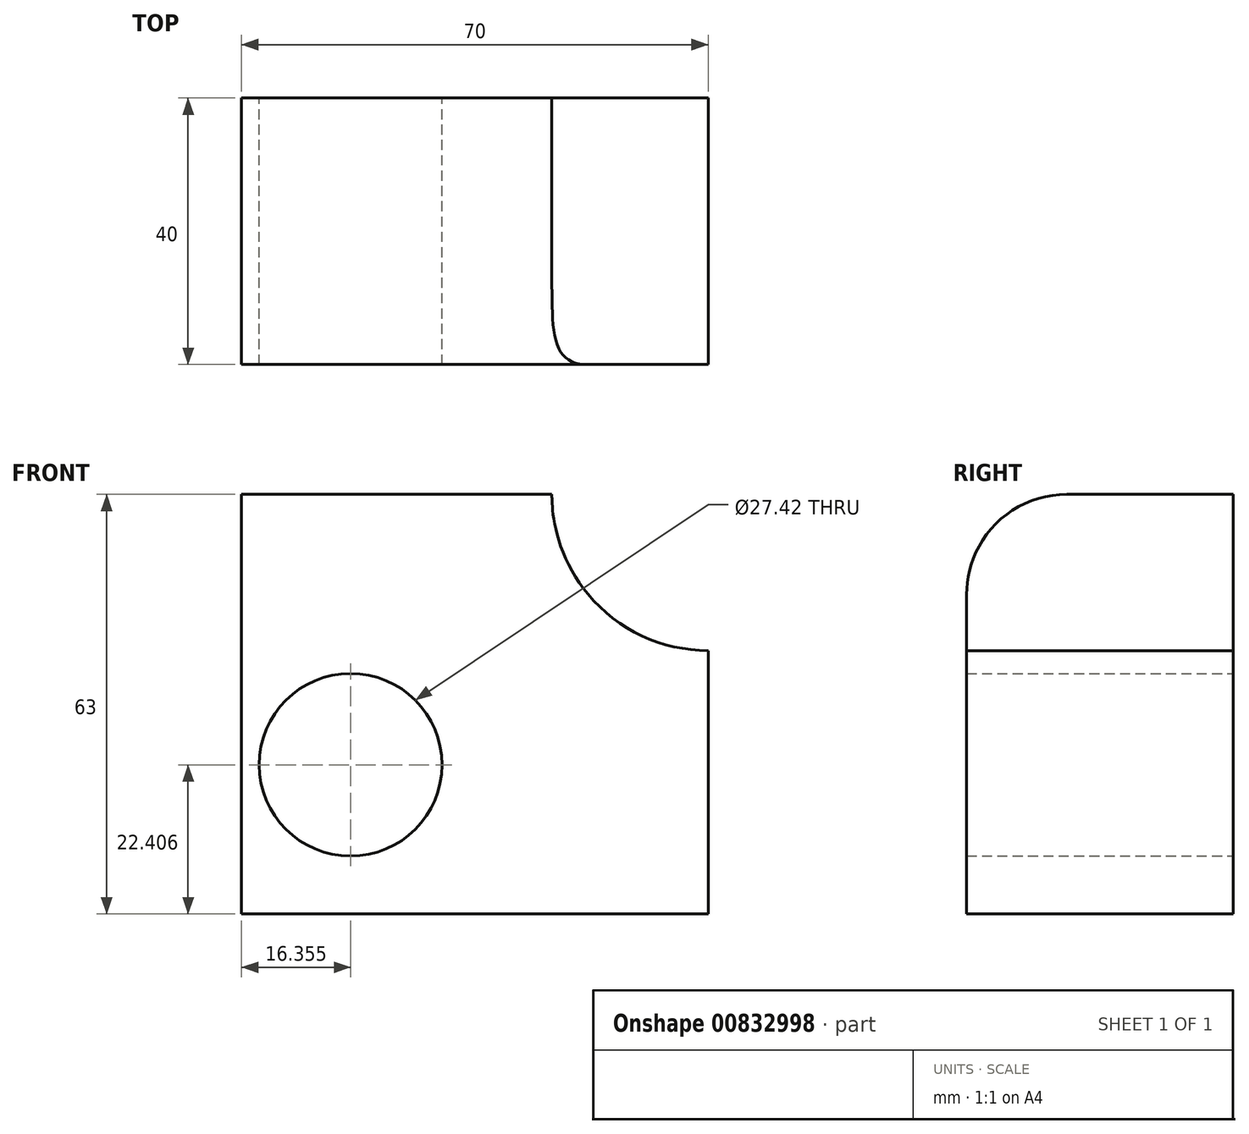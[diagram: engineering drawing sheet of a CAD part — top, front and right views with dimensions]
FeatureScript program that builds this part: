
annotation { "Feature Type Name" : "Feature", "Feature Type Description" : "" }
export const myFeature = defineFeature(function(context is Context, id is Id, definition is map)
    precondition{}
    {
        {
            var Q0;
            Q0=qCreatedBy(makeId("Top.planeOp"),FACE);
            var sketch = newSketch(context, id + "F0", { "sketchPlane" : qUnion([Q0])});
            skLineSegment(sketch, "E0.bottom", {"start": v(-35, -6) * mm, "end": v(35, -6) * mm});
            skLineSegment(sketch, "E0.top", {"start": v(-35, -46) * mm, "end": v(35, -46) * mm});
            skLineSegment(sketch, "E0.left", {"start": v(-35, -6) * mm, "end": v(-35, -46) * mm});
            skLineSegment(sketch, "E0.right", {"start": v(35, -6) * mm, "end": v(35, -46) * mm});
            skSolve(sketch);
        }
        {
            var Q0;
            Q0 = qSketchRegion(id + "F0", true);
            extrude(context, id + "F1", {"entities" : qUnion([Q0]), "depth" : 63 * mm, "offsetDistance" : 25 * mm});
        }
        {
            var Q0;
            Q0=makeQuery(id+"F1.opExtrude","SWEPT_FACE",FACE,{"disambiguationData":[OSD([sQuery(id+"F0.wireOp",EDGE,"E0.top")])]});
            var sketch = newSketch(context, id + "F2", { "sketchPlane" : qUnion([Q0])});
            skCircle(sketch, "E1", {"center": v(35, 63) * mm, "radius": 23.45 * mm});
            skSolve(sketch);
        }
        {
            var Q0;
            Q0 = qSketchRegion(id + "F2", true);
            extrude(context, id + "F3", {"entities" : qUnion([Q0]), "operationType" : NewBodyOperationType.REMOVE, "oppositeDirection" : true, "depth" : 74 * mm, "offsetDistance" : 25 * mm});
        }
        {
            var Q0;
            Q0=qCreatedBy(makeId("Front.planeOp"),FACE);
            var sketch = newSketch(context, id + "F4", { "sketchPlane" : qUnion([Q0])});
            skCircle(sketch, "E2", {"center": v(-18.64, 22.4) * mm, "radius": 13.7 * mm});
            skSolve(sketch);
        }
        {
            var Q0;
            Q0 = qSketchRegion(id + "F4", true);
            extrude(context, id + "F5", {"entities" : qUnion([Q0]), "operationType" : NewBodyOperationType.REMOVE, "depth" : 87.04 * mm, "offsetDistance" : 25 * mm});
        }
        {
            var Q0;
            Q0=makeQuery(id+"F1.opExtrude","CAP_EDGE",EDGE,{"disambiguationData":[OSD([sQuery(id+"F0.wireOp",EDGE,"E0.top")])],"isStart":false});
            fillet(context, id + "F6", {"entities" : qUnion([Q0]), "radius" : 15 * mm, "tangentPropagation" : true, "allowEdgeOverflow" : false});
        }
    });
